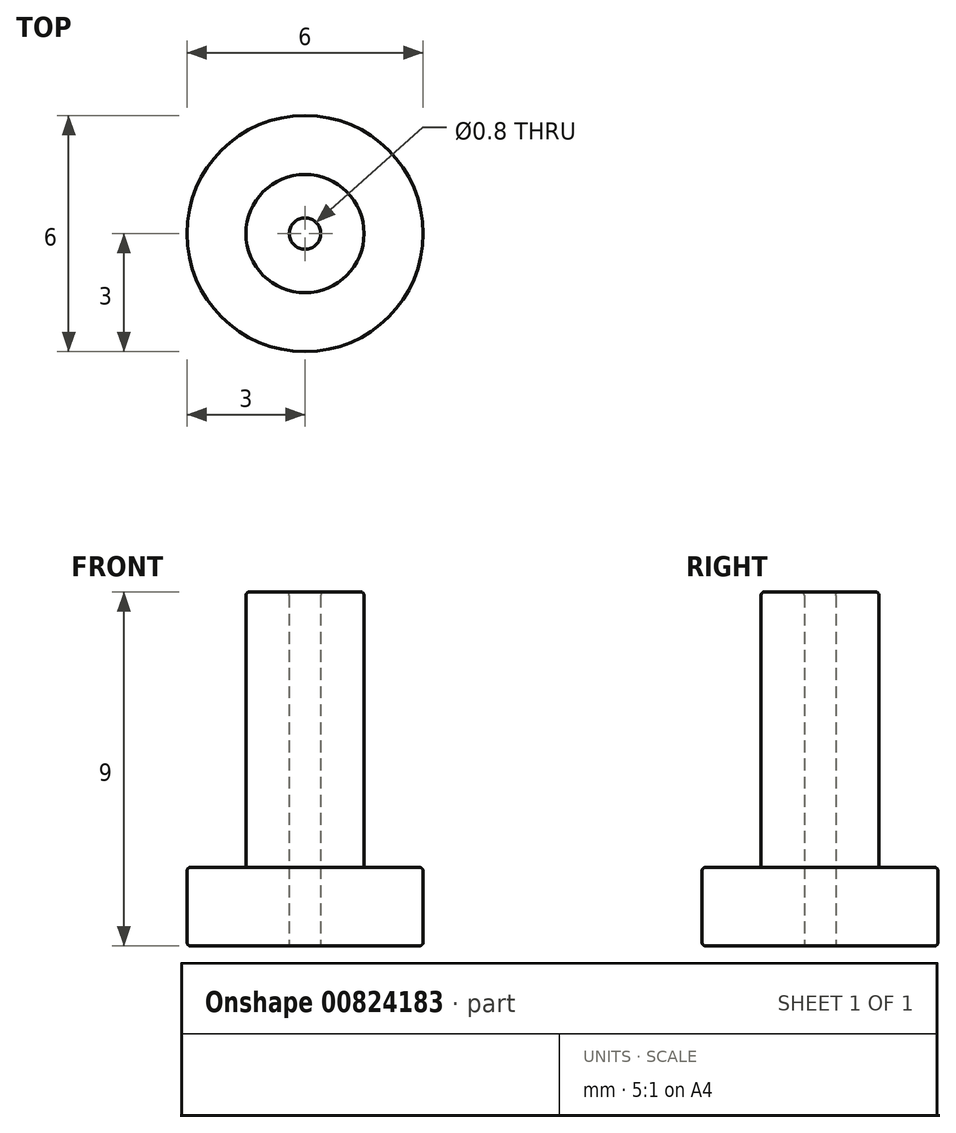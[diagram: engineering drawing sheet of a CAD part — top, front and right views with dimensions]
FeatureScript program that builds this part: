
annotation { "Feature Type Name" : "Feature", "Feature Type Description" : "" }
export const myFeature = defineFeature(function(context is Context, id is Id, definition is map)
    precondition{}
    {
        {
            var Q0;
            Q0=qCreatedBy(makeId("Top.planeOp"),FACE);
            var sketch = newSketch(context, id + "F0", { "sketchPlane" : qUnion([Q0])});
            skCircle(sketch, "E0", {"center": v(0, 0) * mm, "radius": 3 * mm});
            skSolve(sketch);
        }
        {
            var Q0;
            Q0 = qSketchRegion(id + "F0", true);
            extrude(context, id + "F1", {"entities" : qUnion([Q0]), "depth" : 2 * mm, "offsetDistance" : 25 * mm});
        }
        {
            var Q0;
            Q0=makeQuery(id+"F1.opExtrude","CAP_FACE",FACE,{"disambiguationData":[OSD([sQuery(id+"F0.wireOp",EDGE,"E0")])],"isStart":false});
            var sketch = newSketch(context, id + "F2", { "sketchPlane" : qUnion([Q0])});
            skCircle(sketch, "E1", {"center": v(0, 0) * mm, "radius": 1.5 * mm});
            skSolve(sketch);
        }
        {
            var Q0;
            Q0 = qSketchRegion(id + "F2", true);
            extrude(context, id + "F3", {"entities" : qUnion([Q0]), "operationType" : NewBodyOperationType.ADD, "depth" : 7 * mm, "offsetDistance" : 25 * mm});
        }
        {
            var Q0;
            Q0=makeQuery(id+"F1.opExtrude","CAP_FACE",FACE,{"disambiguationData":[OSD([sQuery(id+"F0.wireOp",EDGE,"E0")])],"isStart":true});
            var sketch = newSketch(context, id + "F4", { "sketchPlane" : qUnion([Q0])});
            skCircle(sketch, "E2", {"center": v(0, 0) * mm, "radius": 0.4 * mm});
            skSolve(sketch);
        }
        {
            var Q0;
            Q0 = qSketchRegion(id + "F4", true);
            extrude(context, id + "F5", {"entities" : qUnion([Q0]), "operationType" : NewBodyOperationType.REMOVE, "endBound" : BoundingType.THROUGH_ALL, "oppositeDirection" : true, "depth" : 25 * mm, "offsetDistance" : 25 * mm});
        }
        {
            var Q0;
            Q0=makeQuery(id+"F5.boolean.opBoolean","INTERSECT",EDGE,{"derivedFrom":[makeQuery(id+"F3.opExtrude","CAP_FACE",FACE,{"disambiguationData":[OSD([sQuery(id+"F2.wireOp",EDGE,"E1")])],"isStart":false}),makeQuery(id+"F5.opExtrude","SWEPT_FACE",FACE,{"disambiguationData":[OSD([sQuery(id+"F4.wireOp",EDGE,"E2")])]})]});
            var Q1;
            Q1=makeQuery(id+"F5.boolean.opBoolean","COPY",EDGE,{"derivedFrom":makeQuery(id+"F5.opExtrude","CAP_EDGE",EDGE,{"disambiguationData":[OSD([sQuery(id+"F4.wireOp",EDGE,"E2")])],"isStart":true})});
            var Q2;
            Q2=makeQuery(id+"F1.opExtrude","CAP_EDGE",EDGE,{"disambiguationData":[OSD([sQuery(id+"F0.wireOp",EDGE,"E0")])],"isStart":true});
            var Q3;
            Q3=makeQuery(id+"F1.opExtrude","CAP_EDGE",EDGE,{"disambiguationData":[OSD([sQuery(id+"F0.wireOp",EDGE,"E0")])],"isStart":false});
            var Q4;
            Q4=makeQuery(id+"F3.opExtrude","CAP_EDGE",EDGE,{"disambiguationData":[OSD([sQuery(id+"F2.wireOp",EDGE,"E1")])],"isStart":true});
            var Q5;
            Q5=makeQuery(id+"F3.opExtrude","CAP_EDGE",EDGE,{"disambiguationData":[OSD([sQuery(id+"F2.wireOp",EDGE,"E1")])],"isStart":false});
            fillet(context, id + "F6", {"entities" : qUnion([Q0, Q1, Q2, Q3, Q4, Q5]), "radius" : 0.1 * mm, "tangentPropagation" : true, "allowEdgeOverflow" : false});
        }
    });
